# Revit family: DuraCare-Stool-Payton-
name_source: partatom
category: Furniture
revit_build: Autodesk Revit 2016 (Build: 20150220_1215(x64)
units: mm (PartAtom-declared; Revit-internal decimal feet)

## family parameters
Always vertical = Yes
Cut with Voids When Loaded = No
OmniClass Number = 23.40.20.00
OmniClass Title = General Furniture and Specialties
Room Calculation Point = No
Shared = No
Work Plane-Based = No

## types (2) — shared parameters
Assembly Code = E2020200
Depth = 24"
Keynote = 12500
Low Emitting Finish = Yes
Low Emitting Material = Yes
Manufacturer = DuraCare Seating
Product Documentation Link = https://duracareseating.com
Revit Model Built By = https://servex-us.com
Salvage or Reuse = Yes
Type Comments = Payton Stool
URL = https://duracareseating.com
Width = 23"
zero-valued in all types: Percentage of Recycled Content

## per-type parameters (varying)
| type | Arm Height | Description | FR Height | H 40 | H 45.5 | Height | Seat height |
| CS-734 | 31" | Counter Stool 23"W x 24"D x 40"H - aluminum frame - wood grain finish | 16" | Yes | No | 40" | 24" |
| BS-734 | 37" | Bar Stool 23"W x 24"D x 45.5"H - aluminum frame - wood grain finish | 18" | No | Yes | 45 1/2" | 30" |

note: column(s) folded — value = type name in every type: Model

## geometry (parser evidence)
native form markers: Sweep x9
no freeform markers — native parametric forms only
